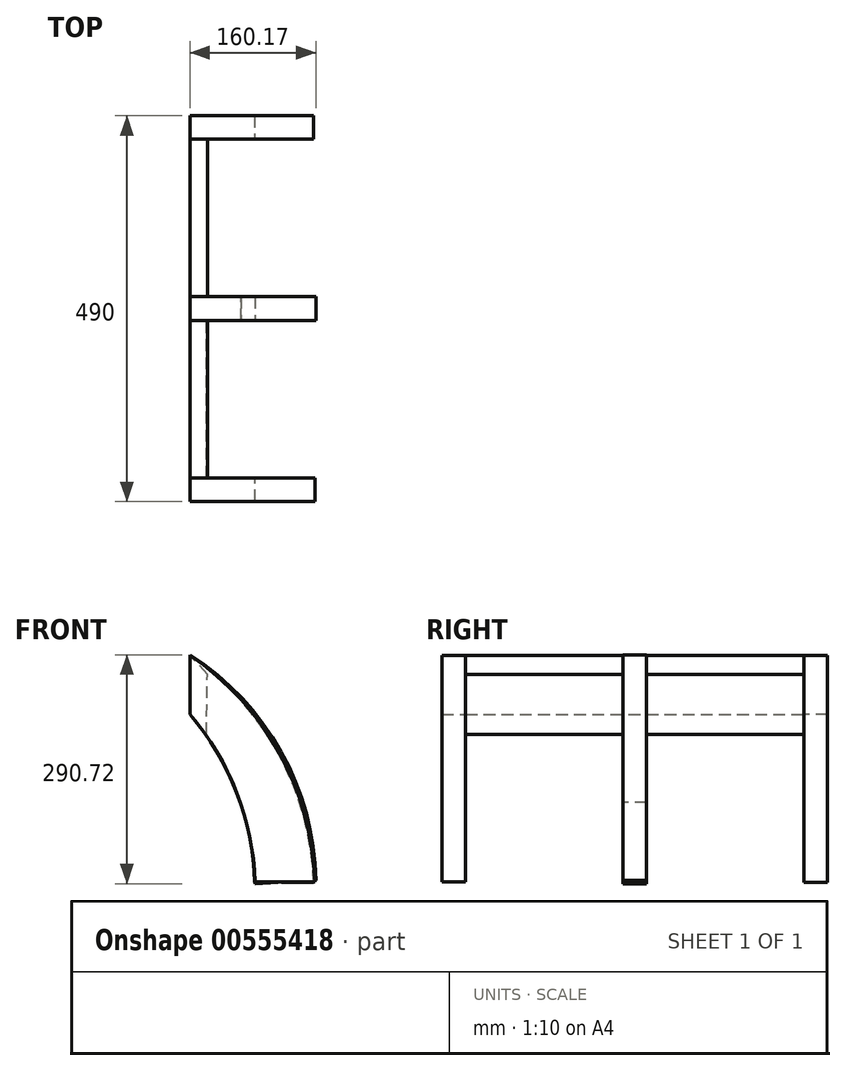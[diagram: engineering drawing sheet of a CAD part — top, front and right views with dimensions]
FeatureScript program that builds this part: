
annotation { "Feature Type Name" : "Feature", "Feature Type Description" : "" }
export const myFeature = defineFeature(function(context is Context, id is Id, definition is map)
    precondition{}
    {
        {
            var Q0;
            Q0=qCreatedBy(makeId("Front.planeOp"),FACE);
            var sketch = newSketch(context, id + "F0", { "sketchPlane" : qUnion([Q0])});
            skArc(sketch, "E0", {"start": v(139.8, 0) * mm, "mid": v(75.37, 97.5) * mm, "end": v(0, 186.8) * mm});
            skLineSegment(sketch, "E1", {"start": v(0, 186.8) * mm, "end": v(0, 111.8) * mm});
            skLineSegment(sketch, "E2", {"start": v(139.8, 0) * mm, "end": v(64.8, 0) * mm});
            skArc(sketch, "E3", {"start": v(64.8, 0) * mm, "mid": v(38.5, 59.43) * mm, "end": v(0, 111.8) * mm});
            skSolve(sketch);
        }
        {
            var Q0;
            Q0=makeQuery(id+"F0.imprint","IMPRINT",FACE,{"disambiguationData":[TD([[makeQuery(id+"F0.imprint","IMPRINT",EDGE,{"derivedFrom":sQuery(id+"F0.wireOp",EDGE,"E0")}),1.0]])]});
            extrude(context, id + "F1", {"entities" : qUnion([Q0]), "depth" : 30 * mm, "offsetDistance" : 25 * mm});
        }
        {
            var Q0;
            Q0=makeQuery(id+"F1.opExtrude","CAP_FACE",FACE,{"disambiguationData":[OSD([sQuery(id+"F0.wireOp",EDGE,"E0"),sQuery(id+"F0.wireOp",EDGE,"E1"),sQuery(id+"F0.wireOp",EDGE,"E2"),sQuery(id+"F0.wireOp",EDGE,"E3")])],"isStart":false});
            var sketch = newSketch(context, id + "F2", { "sketchPlane" : qUnion([Q0])});
            skLineSegment(sketch, "E4", {"start": v(20.94, 86.3) * mm, "end": v(22.32, 162.5) * mm});
            skLineSegment(sketch, "E5", {"start": v(22.32, 162.5) * mm, "end": v(0, 186.8) * mm});
            skLineSegment(sketch, "E6", {"start": v(0, 186.8) * mm, "end": v(0, 111.8) * mm});
            skLineSegment(sketch, "E7", {"start": v(0, 111.8) * mm, "end": v(20.94, 86.3) * mm});
            skSolve(sketch);
        }
        {
            var Q0;
            {var subQ0=sQuery(id+"F2.wireOp",EDGE,"E4");Q0=makeQuery(id+"F2.imprint","IMPRINT",FACE,{"disambiguationData":[TD([[makeQuery(id+"F2.imprint","IMPRINT",EDGE,{"derivedFrom":subQ0}),1.0]])]});}
            extrude(context, id + "F3", {"entities" : qUnion([Q0]), "operationType" : NewBodyOperationType.ADD, "depth" : 200 * mm, "offsetDistance" : 25 * mm});
        }
        {
            var Q0;
            Q0=makeQuery(id+"F1.opExtrude","CAP_FACE",FACE,{"disambiguationData":[OSD([sQuery(id+"F0.wireOp",EDGE,"E0"),sQuery(id+"F0.wireOp",EDGE,"E1"),sQuery(id+"F0.wireOp",EDGE,"E2"),sQuery(id+"F0.wireOp",EDGE,"E3")])],"isStart":true});
            var sketch = newSketch(context, id + "F4", { "sketchPlane" : qUnion([Q0])});
            skLineSegment(sketch, "E8", {"start": v(0, 186.8) * mm, "end": v(0, 111.8) * mm});
            skLineSegment(sketch, "E9", {"start": v(0, 111.8) * mm, "end": v(-20.94, 86.3) * mm});
            skLineSegment(sketch, "E10", {"start": v(-22.32, 162.5) * mm, "end": v(0, 186.8) * mm});
            skLineSegment(sketch, "E11", {"start": v(-22.32, 162.5) * mm, "end": v(-20.94, 86.3) * mm});
            skSolve(sketch);
        }
        {
            var Q0;
            {var subQ0=sQuery(id+"F4.wireOp",EDGE,"E8");Q0=makeQuery(id+"F4.imprint","IMPRINT",FACE,{"disambiguationData":[TD([[makeQuery(id+"F4.imprint","IMPRINT",EDGE,{"derivedFrom":subQ0}),-1.0]])]});}
            extrude(context, id + "F5", {"entities" : qUnion([Q0]), "operationType" : NewBodyOperationType.ADD, "depth" : 200 * mm, "offsetDistance" : 25 * mm});
        }
        {
            var Q0;
            Q0=makeQuery(id+"F5.opExtrude","CAP_FACE",FACE,{"disambiguationData":[OSD([sQuery(id+"F0.wireOp",EDGE,"E3"),sQuery(id+"F4.wireOp",EDGE,"E8"),sQuery(id+"F4.wireOp",EDGE,"E10"),sQuery(id+"F4.wireOp",EDGE,"E11")])],"isStart":false});
            var sketch = newSketch(context, id + "F6", { "sketchPlane" : qUnion([Q0])});
            skLineSegment(sketch, "E12", {"start": v(0, 186.8) * mm, "end": v(0, 111.8) * mm});
            skArc(sketch, "E13", {"start": v(0, 111.8) * mm, "mid": v(-59.44, 12.1) * mm, "end": v(-82.29, -101.72) * mm});
            skLineSegment(sketch, "E14", {"start": v(-82.29, -101.72) * mm, "end": v(-157.29, -101.72) * mm});
            skArc(sketch, "E15", {"start": v(0, 186.8) * mm, "mid": v(-112.9, 61.21) * mm, "end": v(-157.29, -101.72) * mm});
            skSolve(sketch);
        }
        {
            var Q0;
            Q0=makeQuery(id+"F6.imprint","IMPRINT",FACE,{"disambiguationData":[TD([[makeQuery(id+"F6.imprint","IMPRINT",EDGE,{"derivedFrom":sQuery(id+"F6.wireOp",EDGE,"E13")}),-1.0]])]});
            var Q1;
            Q1=makeQuery(id+"F6.imprint","IMPRINT",FACE,{"disambiguationData":[TD([[makeQuery(id+"F6.imprint","IMPRINT",EDGE,{"derivedFrom":sQuery(id+"F6.wireOp",EDGE,"E12")}),-1.0]])]});
            extrude(context, id + "F7", {"entities" : qUnion([Q0, Q1]), "operationType" : NewBodyOperationType.ADD, "depth" : 30 * mm, "offsetDistance" : 25 * mm});
        }
        {
            var Q0;
            Q0=makeQuery(id+"F3.opExtrude","CAP_FACE",FACE,{"disambiguationData":[OSD([sQuery(id+"F0.wireOp",EDGE,"E3"),sQuery(id+"F2.wireOp",EDGE,"E4"),sQuery(id+"F2.wireOp",EDGE,"E5"),sQuery(id+"F2.wireOp",EDGE,"E6")])],"isStart":false});
            var sketch = newSketch(context, id + "F8", { "sketchPlane" : qUnion([Q0])});
            skArc(sketch, "E16", {"start": v(158.75, -101.4) * mm, "mid": v(114.05, 61.8) * mm, "end": v(0, 186.8) * mm});
            skArc(sketch, "E17", {"start": v(82.96, -101.4) * mm, "mid": v(59.58, 12.25) * mm, "end": v(0, 111.8) * mm});
            skLineSegment(sketch, "E18", {"start": v(0, 186.8) * mm, "end": v(0, 111.8) * mm});
            skLineSegment(sketch, "E19", {"start": v(82.96, -101.4) * mm, "end": v(158.75, -101.4) * mm});
            skSolve(sketch);
        }
        {
            var Q0;
            Q0=makeQuery(id+"F8.imprint","IMPRINT",FACE,{"disambiguationData":[TD([[makeQuery(id+"F8.imprint","IMPRINT",EDGE,{"derivedFrom":sQuery(id+"F8.wireOp",EDGE,"E16")}),1.0]])]});
            var Q1;
            Q1=makeQuery(id+"F8.imprint","IMPRINT",FACE,{"disambiguationData":[TD([[makeQuery(id+"F8.imprint","IMPRINT",EDGE,{"derivedFrom":sQuery(id+"F8.wireOp",EDGE,"E18")}),1.0]])]});
            extrude(context, id + "F9", {"entities" : qUnion([Q0, Q1]), "operationType" : NewBodyOperationType.ADD, "depth" : 30 * mm, "offsetDistance" : 25 * mm});
        }
        {
            var Q0;
            {var subQ0=sQuery(id+"F0.wireOp",EDGE,"E2");var subQ1=sQuery(id+"F0.wireOp",EDGE,"E3");var subQ2=sQuery(id+"F0.wireOp",EDGE,"E0");var subQ3=makeQuery(id+"F1.opExtrude","CAP_FACE",FACE,{"disambiguationData":[OSD([subQ2,sQuery(id+"F0.wireOp",EDGE,"E1"),subQ0,subQ1])],"isStart":false});Q0=makeQuery(id+"F3.boolean.opBoolean","SPLIT",FACE,{"disambiguationData":[TD([makeQuery(id+"F1.opExtrude","SWEPT_FACE",FACE,{"disambiguationData":[OSD([subQ0])]})])],"derivedFrom":subQ3});}
            var sketch = newSketch(context, id + "F10", { "sketchPlane" : qUnion([Q0])});
            skArc(sketch, "E20", {"start": v(160.17, -99.29) * mm, "mid": v(116, 64.01) * mm, "end": v(0, 187.14) * mm});
            skArc(sketch, "E21", {"start": v(83.02, -103.58) * mm, "mid": v(60.73, 12.36) * mm, "end": v(0, 113.6) * mm});
            skLineSegment(sketch, "E22", {"start": v(0, 187.14) * mm, "end": v(0, 113.6) * mm});
            skLineSegment(sketch, "E23", {"start": v(83.02, -103.58) * mm, "end": v(160.17, -99.29) * mm});
            skSolve(sketch);
        }
        {
            var Q0;
            Q0=makeQuery(id+"F10.imprint","IMPRINT",FACE,{"disambiguationData":[TD([[makeQuery(id+"F10.imprint","IMPRINT",EDGE,{"derivedFrom":sQuery(id+"F10.wireOp",EDGE,"E20")}),1.0]])]});
            extrude(context, id + "F11", {"entities" : qUnion([Q0]), "operationType" : NewBodyOperationType.ADD, "oppositeDirection" : true, "depth" : 30 * mm, "offsetDistance" : 25 * mm});
        }
    });
